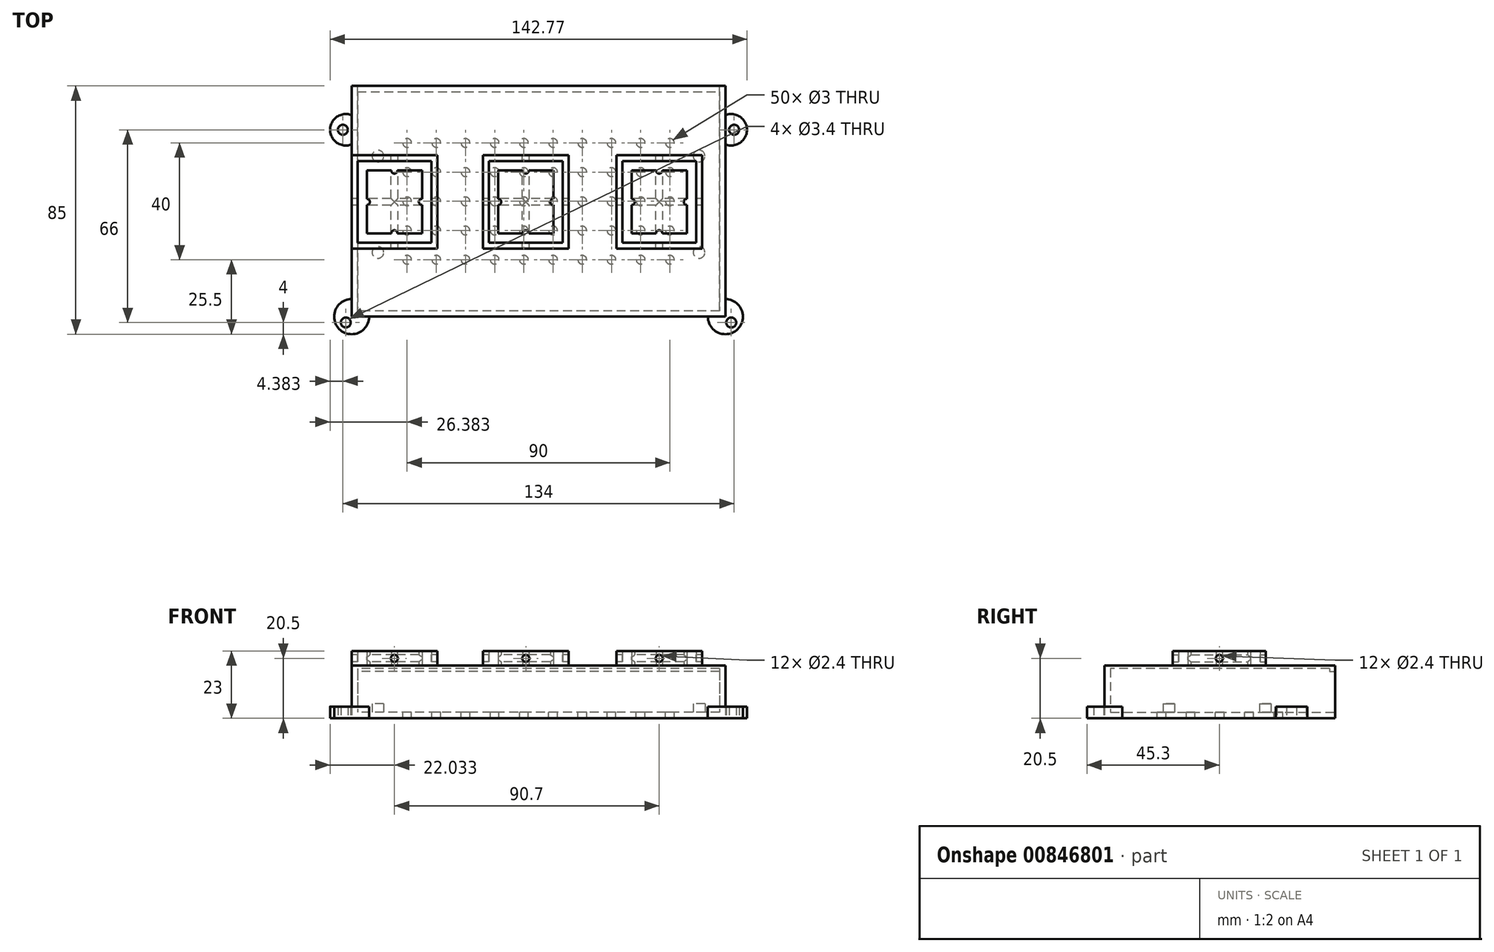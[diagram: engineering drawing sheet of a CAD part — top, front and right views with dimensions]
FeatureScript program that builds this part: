
annotation { "Feature Type Name" : "Feature", "Feature Type Description" : "" }
export const myFeature = defineFeature(function(context is Context, id is Id, definition is map)
    precondition{}
    {
        {
            var Q0;
            Q0=qCreatedBy(makeId("Top.planeOp"),FACE);
            var sketch = newSketch(context, id + "F0", { "sketchPlane" : qUnion([Q0])});
            skLineSegment(sketch, "E0.bottom", {"start": v(63.95, -38.95) * mm, "end": v(-60.05, -38.95) * mm});
            skLineSegment(sketch, "E0.top", {"start": v(63.95, 36.05) * mm, "end": v(-60.05, 36.05) * mm});
            skLineSegment(sketch, "E0.left", {"start": v(63.95, -38.95) * mm, "end": v(63.95, 36.05) * mm});
            skLineSegment(sketch, "E0.right", {"start": v(-60.05, -38.95) * mm, "end": v(-60.05, 36.05) * mm});
            skCircle(sketch, "E1", {"center": v(-53.05, 14.05) * mm, "radius": 2 * mm});
            skCircle(sketch, "E2", {"center": v(-53.05, -18.95) * mm, "radius": 2 * mm});
            skCircle(sketch, "E3", {"center": v(56.95, -18.95) * mm, "radius": 2 * mm});
            skCircle(sketch, "E4", {"center": v(56.95, 14.05) * mm, "radius": 2 * mm});
            skLineSegment(sketch, "E5.bottom", {"start": v(65.95, -40.95) * mm, "end": v(-62.05, -40.95) * mm});
            skLineSegment(sketch, "E5.top", {"start": v(65.95, 38.05) * mm, "end": v(-62.05, 38.05) * mm});
            skLineSegment(sketch, "E5.left", {"start": v(65.95, -40.95) * mm, "end": v(65.95, 38.05) * mm});
            skLineSegment(sketch, "E5.right", {"start": v(-62.05, -40.95) * mm, "end": v(-62.05, 38.05) * mm});
            skArc(sketch, "E6", {"start": v(59.95, -40.95) * mm, "mid": v(70.2, -45.2) * mm, "end": v(65.95, -34.95) * mm});
            skArc(sketch, "E7", {"start": v(-62.05, -34.95) * mm, "mid": v(-66.29, -45.2) * mm, "end": v(-56.05, -40.95) * mm});
            skPoint(sketch, "E8", {"position": v(67.95, -42.95) * mm});
            skPoint(sketch, "E9", {"position": v(-64.05, -42.95) * mm});
            skArc(sketch, "E10", {"start": v(-62.05, 28.05) * mm, "mid": v(-69.43, 23.05) * mm, "end": v(-62.05, 18.05) * mm});
            skArc(sketch, "E11", {"start": v(65.95, 18.05) * mm, "mid": v(73.34, 23.05) * mm, "end": v(65.95, 28.05) * mm});
            skPoint(sketch, "E12", {"position": v(-65.05, 23.05) * mm});
            skPoint(sketch, "E13", {"position": v(68.95, 23.05) * mm});
            skSolve(sketch);
        }
        {
            var Q0;
            Q0=makeQuery(id+"F0.imprint","IMPRINT",FACE,{"disambiguationData":[TD([[makeQuery(id+"F0.imprint","IMPRINT",EDGE,{"derivedFrom":sQuery(id+"F0.wireOp",EDGE,"E0.bottom")}),-1.0]])]});
            extrude(context, id + "F1", {"entities" : qUnion([Q0]), "depth" : 2 * mm, "offsetDistance" : 25 * mm});
        }
        {
            var Q0;
            Q0=makeQuery(id+"F0.imprint","IMPRINT",FACE,{"disambiguationData":[TD([[makeQuery(id+"F0.imprint","IMPRINT",EDGE,{"derivedFrom":sQuery(id+"F0.wireOp",EDGE,"E0.bottom")}),1.0]])]});
            extrude(context, id + "F2", {"entities" : qUnion([Q0]), "operationType" : NewBodyOperationType.ADD, "depth" : 18 * mm, "offsetDistance" : 25 * mm});
        }
        {
            var Q0;
            Q0=makeQuery(id+"F2.opExtrude","SWEPT_FACE",FACE,{"disambiguationData":[OSD([sQuery(id+"F0.wireOp",EDGE,"E5.top")])]});
            var sketch = newSketch(context, id + "F3", { "sketchPlane" : qUnion([Q0])});
            skLineSegment(sketch, "E14.bottom", {"start": v(-63.95, 16) * mm, "end": v(60.05, 16) * mm});
            skLineSegment(sketch, "E14.top", {"start": v(-63.95, 2) * mm, "end": v(60.05, 2) * mm});
            skLineSegment(sketch, "E14.left", {"start": v(-63.95, 16) * mm, "end": v(-63.95, 2) * mm});
            skLineSegment(sketch, "E14.right", {"start": v(60.05, 16) * mm, "end": v(60.05, 2) * mm});
            skSolve(sketch);
        }
        {
            var Q0;
            Q0=makeQuery(id+"F3.imprint","IMPRINT",FACE,{"disambiguationData":[TD([[makeQuery(id+"F3.imprint","IMPRINT",EDGE,{"derivedFrom":sQuery(id+"F3.wireOp",EDGE,"E14.bottom")}),-1.0]])]});
            extrude(context, id + "F4", {"entities" : qUnion([Q0]), "operationType" : NewBodyOperationType.REMOVE, "endBound" : BoundingType.UP_TO_NEXT, "oppositeDirection" : true, "depth" : 25 * mm, "offsetDistance" : 25 * mm});
        }
        {
            var Q0;
            Q0=makeQuery(id+"F0.imprint","IMPRINT",FACE,{"disambiguationData":[TD([[makeQuery(id+"F0.imprint","IMPRINT",EDGE,{"derivedFrom":sQuery(id+"F0.wireOp",EDGE,"E1")}),1.0]])]});
            var Q1;
            Q1=makeQuery(id+"F0.imprint","IMPRINT",FACE,{"disambiguationData":[TD([[makeQuery(id+"F0.imprint","IMPRINT",EDGE,{"derivedFrom":sQuery(id+"F0.wireOp",EDGE,"E2")}),1.0]])]});
            var Q2;
            Q2=makeQuery(id+"F0.imprint","IMPRINT",FACE,{"disambiguationData":[TD([[makeQuery(id+"F0.imprint","IMPRINT",EDGE,{"derivedFrom":sQuery(id+"F0.wireOp",EDGE,"E3")}),1.0]])]});
            var Q3;
            Q3=makeQuery(id+"F0.imprint","IMPRINT",FACE,{"disambiguationData":[TD([[makeQuery(id+"F0.imprint","IMPRINT",EDGE,{"derivedFrom":sQuery(id+"F0.wireOp",EDGE,"E4")}),1.0]])]});
            extrude(context, id + "F5", {"entities" : qUnion([Q0, Q1, Q2, Q3]), "operationType" : NewBodyOperationType.ADD, "depth" : 5 * mm, "offsetDistance" : 25 * mm});
        }
        {
            var Q0;
            Q0=makeQuery(id+"F2.opExtrude","SWEPT_FACE",FACE,{"disambiguationData":[OSD([sQuery(id+"F0.wireOp",EDGE,"E0.bottom")])]});
            var sketch = newSketch(context, id + "F6", { "sketchPlane" : qUnion([Q0])});
            skLineSegment(sketch, "E15.bottom", {"start": v(-63.95, 18) * mm, "end": v(60.05, 18) * mm});
            skLineSegment(sketch, "E15.top", {"start": v(-63.95, 17) * mm, "end": v(60.05, 17) * mm});
            skLineSegment(sketch, "E15.left", {"start": v(-63.95, 18) * mm, "end": v(-63.95, 17) * mm});
            skLineSegment(sketch, "E15.right", {"start": v(60.05, 18) * mm, "end": v(60.05, 17) * mm});
            skSolve(sketch);
        }
        {
            var Q0;
            Q0=makeQuery(id+"F6.imprint","IMPRINT",FACE,{"disambiguationData":[TD([[makeQuery(id+"F6.imprint","IMPRINT",EDGE,{"derivedFrom":sQuery(id+"F6.wireOp",EDGE,"E15.bottom")}),-1.0]])]});
            extrude(context, id + "F7", {"entities" : qUnion([Q0]), "operationType" : NewBodyOperationType.ADD, "endBound" : BoundingType.UP_TO_NEXT, "depth" : 25 * mm, "offsetDistance" : 25 * mm});
        }
        {
            var Q0;
            Q0=makeQuery(id+"F7.boolean.opBoolean","MERGE",FACE,{"derivedFrom":[makeQuery(id+"F2.opExtrude","CAP_FACE",FACE,{"disambiguationData":[OSD([sQuery(id+"F0.wireOp",EDGE,"E0.bottom"),sQuery(id+"F0.wireOp",EDGE,"E0.top"),sQuery(id+"F0.wireOp",EDGE,"E0.left"),sQuery(id+"F0.wireOp",EDGE,"E0.right"),sQuery(id+"F0.wireOp",EDGE,"E5.bottom"),sQuery(id+"F0.wireOp",EDGE,"E5.top"),sQuery(id+"F0.wireOp",EDGE,"E5.left"),sQuery(id+"F0.wireOp",EDGE,"E5.right")])],"isStart":false}),makeQuery(id+"F7.opExtrude","SWEPT_FACE",FACE,{"disambiguationData":[OSD([sQuery(id+"F6.wireOp",EDGE,"E15.bottom")])]})]});
            var sketch = newSketch(context, id + "F8", { "sketchPlane" : qUnion([Q0])});
            skLineSegment(sketch, "E16.bottom", {"start": v(-15.05, 12.3) * mm, "end": v(10.25, 12.3) * mm});
            skLineSegment(sketch, "E16.top", {"start": v(-15.05, -15.6) * mm, "end": v(10.25, -15.6) * mm});
            skLineSegment(sketch, "E16.left", {"start": v(-15.05, 12.3) * mm, "end": v(-15.05, -15.6) * mm});
            skLineSegment(sketch, "E16.right", {"start": v(10.25, 12.3) * mm, "end": v(10.25, -15.6) * mm});
            skLineSegment(sketch, "E17.bottom", {"start": v(-11.85, 9.1) * mm, "end": v(7.05, 9.1) * mm});
            skLineSegment(sketch, "E17.top", {"start": v(-11.85, -12.4) * mm, "end": v(7.05, -12.4) * mm});
            skLineSegment(sketch, "E17.left", {"start": v(-11.85, 9.1) * mm, "end": v(-11.85, -12.4) * mm});
            skLineSegment(sketch, "E17.right", {"start": v(7.05, 9.1) * mm, "end": v(7.05, -12.4) * mm});
            skLineSegment(sketch, "E18.bottom", {"start": v(30.65, 12.3) * mm, "end": v(55.95, 12.3) * mm});
            skLineSegment(sketch, "E18.top", {"start": v(30.65, -15.6) * mm, "end": v(55.95, -15.6) * mm});
            skLineSegment(sketch, "E18.left", {"start": v(30.65, 12.3) * mm, "end": v(30.65, -15.6) * mm});
            skLineSegment(sketch, "E18.right", {"start": v(55.95, 12.3) * mm, "end": v(55.95, -15.6) * mm});
            skLineSegment(sketch, "E19.bottom", {"start": v(33.85, 9.1) * mm, "end": v(52.75, 9.1) * mm});
            skLineSegment(sketch, "E19.top", {"start": v(33.85, -12.4) * mm, "end": v(52.75, -12.4) * mm});
            skLineSegment(sketch, "E19.left", {"start": v(33.85, 9.1) * mm, "end": v(33.85, -12.4) * mm});
            skLineSegment(sketch, "E19.right", {"start": v(52.75, 9.1) * mm, "end": v(52.75, -12.4) * mm});
            skCircle(sketch, "E20", {"center": v(-2.4, 9.1) * mm, "radius": 1.05 * mm});
            skLineSegment(sketch, "E21.bottom", {"start": v(-17.05, 14.3) * mm, "end": v(12.25, 14.3) * mm});
            skLineSegment(sketch, "E21.top", {"start": v(-17.05, -17.6) * mm, "end": v(12.25, -17.6) * mm});
            skLineSegment(sketch, "E21.left", {"start": v(-17.05, 14.3) * mm, "end": v(-17.05, -17.6) * mm});
            skLineSegment(sketch, "E21.right", {"start": v(12.25, 14.3) * mm, "end": v(12.25, -17.6) * mm});
            skLineSegment(sketch, "E22.bottom", {"start": v(28.65, 14.3) * mm, "end": v(57.95, 14.3) * mm});
            skLineSegment(sketch, "E22.top", {"start": v(28.65, -17.6) * mm, "end": v(57.95, -17.6) * mm});
            skLineSegment(sketch, "E22.left", {"start": v(28.65, 14.3) * mm, "end": v(28.65, -17.6) * mm});
            skLineSegment(sketch, "E22.right", {"start": v(57.95, 14.3) * mm, "end": v(57.95, -17.6) * mm});
            skCircle(sketch, "E23", {"center": v(7.05, -1.65) * mm, "radius": 1.05 * mm});
            skCircle(sketch, "E24", {"center": v(-2.4, -12.4) * mm, "radius": 1.05 * mm});
            skCircle(sketch, "E25", {"center": v(-11.85, -1.65) * mm, "radius": 1.05 * mm});
            skCircle(sketch, "E26", {"center": v(33.85, -1.65) * mm, "radius": 1.05 * mm});
            skCircle(sketch, "E27", {"center": v(43.3, -12.4) * mm, "radius": 1.05 * mm});
            skCircle(sketch, "E28", {"center": v(52.75, -1.65) * mm, "radius": 1.05 * mm});
            skCircle(sketch, "E29", {"center": v(43.3, 9.1) * mm, "radius": 1.05 * mm});
            skLineSegment(sketch, "E30.1.0.0", {"start": v(-56.85, 9.1) * mm, "end": v(-37.95, 9.1) * mm});
            skLineSegment(sketch, "E30.1.0.1", {"start": v(-32.75, 14.3) * mm, "end": v(-32.75, -17.6) * mm});
            skLineSegment(sketch, "E30.1.0.2", {"start": v(-62.05, -17.6) * mm, "end": v(-32.75, -17.6) * mm});
            skLineSegment(sketch, "E30.1.0.3", {"start": v(-56.85, 9.1) * mm, "end": v(-56.85, -12.4) * mm});
            skLineSegment(sketch, "E30.1.0.4", {"start": v(-62.05, 14.3) * mm, "end": v(-32.75, 14.3) * mm});
            skLineSegment(sketch, "E30.1.0.5", {"start": v(-62.05, 14.3) * mm, "end": v(-62.05, -17.6) * mm});
            skLineSegment(sketch, "E30.1.0.6", {"start": v(-56.85, -12.4) * mm, "end": v(-37.95, -12.4) * mm});
            skLineSegment(sketch, "E30.1.0.7", {"start": v(-37.95, 9.1) * mm, "end": v(-37.95, -12.4) * mm});
            skLineSegment(sketch, "E30.1.0.8", {"start": v(-34.75, 12.3) * mm, "end": v(-34.75, -15.6) * mm});
            skLineSegment(sketch, "E30.1.0.9", {"start": v(-60.05, 12.3) * mm, "end": v(-34.75, 12.3) * mm});
            skLineSegment(sketch, "E30.1.0.10", {"start": v(-60.05, 12.3) * mm, "end": v(-60.05, -15.6) * mm});
            skLineSegment(sketch, "E30.1.0.11", {"start": v(-60.05, -15.6) * mm, "end": v(-34.75, -15.6) * mm});
            skCircle(sketch, "E30.1.0.12", {"center": v(-56.85, -1.65) * mm, "radius": 1.05 * mm});
            skCircle(sketch, "E30.1.0.13", {"center": v(-47.4, -12.4) * mm, "radius": 1.05 * mm});
            skCircle(sketch, "E30.1.0.14", {"center": v(-37.95, -1.65) * mm, "radius": 1.05 * mm});
            skCircle(sketch, "E30.1.0.15", {"center": v(-47.4, 9.1) * mm, "radius": 1.05 * mm});
            skLineSegment(sketch, "E30.direction1", {"start": v(-17.05, -17.6) * mm, "end": v(-62.05, -17.6) * mm, "construction": true});
            skSolve(sketch);
        }
        {
            var Q0;
            Q0=makeQuery(id+"F8.imprint","IMPRINT",FACE,{"disambiguationData":[TD([[makeQuery(id+"F8.imprint","IMPRINT",EDGE,{"derivedFrom":sQuery(id+"F8.wireOp",EDGE,"E16.bottom")}),1.0]])]});
            var Q1;
            {var subQ1=sQuery(id+"F8.wireOp",EDGE,"E17.bottom");var subQ4=sQuery(id+"F8.wireOp",EDGE,"E17.left");var subQ5=makeQuery(id+"F8.imprint","INTERSECT",VERTEX,{"derivedFrom":[subQ1,subQ4]});Q1=makeQuery(id+"F8.imprint","IMPRINT",FACE,{"disambiguationData":[TD([[makeQuery(id+"F8.imprint","IMPRINT",EDGE,{"disambiguationData":[TD([[subQ5,-1.0]])],"derivedFrom":subQ1}),-1.0]])]});}
            var Q2;
            {var subQ1=sQuery(id+"F8.wireOp",EDGE,"E19.left");var subQ4=sQuery(id+"F8.wireOp",EDGE,"E19.bottom");var subQ5=makeQuery(id+"F8.imprint","INTERSECT",VERTEX,{"derivedFrom":[subQ4,subQ1]});Q2=makeQuery(id+"F8.imprint","IMPRINT",FACE,{"disambiguationData":[TD([[makeQuery(id+"F8.imprint","IMPRINT",EDGE,{"disambiguationData":[TD([[subQ5,-1.0]])],"derivedFrom":subQ4}),-1.0]])]});}
            var Q3;
            Q3=makeQuery(id+"F8.imprint","IMPRINT",FACE,{"disambiguationData":[TD([[makeQuery(id+"F8.imprint","IMPRINT",EDGE,{"derivedFrom":sQuery(id+"F8.wireOp",EDGE,"E18.bottom")}),1.0]])]});
            var Q4;
            {var subQ8=sQuery(id+"F8.wireOp",EDGE,"E30.1.0.3");var subQ13=sQuery(id+"F8.wireOp",EDGE,"E30.1.0.0");var subQ14=makeQuery(id+"F8.imprint","INTERSECT",VERTEX,{"derivedFrom":[subQ13,subQ8]});Q4=makeQuery(id+"F8.imprint","IMPRINT",FACE,{"disambiguationData":[TD([[makeQuery(id+"F8.imprint","IMPRINT",EDGE,{"disambiguationData":[TD([[subQ14,-1.0]])],"derivedFrom":subQ13}),-1.0]])]});}
            var Q5;
            Q5=makeQuery(id+"F8.imprint","IMPRINT",FACE,{"disambiguationData":[TD([[makeQuery(id+"F8.imprint","IMPRINT",EDGE,{"derivedFrom":sQuery(id+"F8.wireOp",EDGE,"E30.1.0.1")}),-1.0]])]});
            extrude(context, id + "F9", {"entities" : qUnion([Q0, Q1, Q2, Q3, Q4, Q5]), "operationType" : NewBodyOperationType.ADD, "depth" : 5 * mm, "offsetDistance" : 25 * mm});
        }
        {
            var Q0;
            {var subQ3=sQuery(id+"F0.wireOp",EDGE,"mSIi04YN-kxax-JNjT-FgOG-nQ7TCZ75OfZn");Q0=makeQuery(id+"F0.imprint","IMPRINT",FACE,{"disambiguationData":[TD([[makeQuery(id+"F0.imprint","IMPRINT",EDGE,{"derivedFrom":subQ3}),1.0]])]});}
            var Q1;
            {var subQ3=sQuery(id+"F0.wireOp",EDGE,"E7");Q1=makeQuery(id+"F0.imprint","IMPRINT",FACE,{"disambiguationData":[TD([[makeQuery(id+"F0.imprint","IMPRINT",EDGE,{"derivedFrom":subQ3}),1.0]])]});}
            var Q2;
            {var subQ3=sQuery(id+"F0.wireOp",EDGE,"E6");Q2=makeQuery(id+"F0.imprint","IMPRINT",FACE,{"disambiguationData":[TD([[makeQuery(id+"F0.imprint","IMPRINT",EDGE,{"derivedFrom":subQ3}),1.0]])]});}
            var Q3;
            {var subQ3=sQuery(id+"F0.wireOp",EDGE,"2plFA931-hQRt-3nQC-mfBG-ZgZCNlgZvkkJ");Q3=makeQuery(id+"F0.imprint","IMPRINT",FACE,{"disambiguationData":[TD([[makeQuery(id+"F0.imprint","IMPRINT",EDGE,{"derivedFrom":subQ3}),1.0]])]});}
            var Q4;
            {var subQ0=sQuery(id+"F0.wireOp",EDGE,"E11");Q4=makeQuery(id+"F0.imprint","IMPRINT",FACE,{"disambiguationData":[TD([[makeQuery(id+"F0.imprint","IMPRINT",EDGE,{"derivedFrom":subQ0}),1.0]])]});}
            var Q5;
            {var subQ0=sQuery(id+"F0.wireOp",EDGE,"E10");Q5=makeQuery(id+"F0.imprint","IMPRINT",FACE,{"disambiguationData":[TD([[makeQuery(id+"F0.imprint","IMPRINT",EDGE,{"derivedFrom":subQ0}),1.0]])]});}
            extrude(context, id + "F10", {"entities" : qUnion([Q0, Q1, Q2, Q3, Q4, Q5]), "operationType" : NewBodyOperationType.ADD, "depth" : 4 * mm, "offsetDistance" : 25 * mm});
        }
        {
            var Q0;
            Q0=sQuery(id+"F0.wireOp",VERTEX,"E9");
            var Q1;
            Q1=sQuery(id+"F0.wireOp",VERTEX,"E8");
            var Q2;
            Q2=sQuery(id+"F0.wireOp",VERTEX,"c99c4bf4-b353-43c5-8701-cd882d36ad5d");
            var Q3;
            Q3=sQuery(id+"F0.wireOp",VERTEX,"7333e0a9-a8a0-4818-a494-4a8ed08a8f91");
            var Q4;
            Q4=sQuery(id+"F0.wireOp",VERTEX,"E13");
            var Q5;
            Q5=sQuery(id+"F0.wireOp",VERTEX,"E12");
            var Q6;
            Q6=makeQuery(id+"F1.opExtrude","SWEPT_BODY",BODY,{"disambiguationData":[OSD([sQuery(id+"F0.wireOp",EDGE,"E0.bottom"),sQuery(id+"F0.wireOp",EDGE,"E0.top"),sQuery(id+"F0.wireOp",EDGE,"E0.left"),sQuery(id+"F0.wireOp",EDGE,"E0.right"),sQuery(id+"F0.wireOp",EDGE,"E1"),sQuery(id+"F0.wireOp",EDGE,"E2"),sQuery(id+"F0.wireOp",EDGE,"E3"),sQuery(id+"F0.wireOp",EDGE,"E4")])]});
            hole(context, id + "F11", {"style" : HoleStyle.SIMPLE, "endStyle" : HoleEndStyle.THROUGH, "oppositeDirection" : true, "standardTappedOrClearance" : lookupTablePath({ "fit" : "Normal", "standard" : "ISO", "size" : "M3", "type" : "Clearance" }), "standardBlindInLast" : lookupTablePath({ "fit" : "Normal", "standard" : "ISO", "size" : "M3", "type" : "Clearance" }), "holeDiameter" : 3.4 * mm, "majorDiameter" : 5 * mm, "isTappedThrough" : true, "tappedDepth" : 12 * mm, "tapClearance" : 3, "locations" : qUnion([Q0, Q1, Q2, Q3, Q4, Q5]), "scope" : qUnion([Q6])});
        }
        {
            var Q0;
            Q0=makeQuery(id+"F9.boolean.opBoolean","MERGE",FACE,{"derivedFrom":[makeQuery(id+"F2.opExtrude","SWEPT_FACE",FACE,{"disambiguationData":[OSD([sQuery(id+"F0.wireOp",EDGE,"E5.right")])]}),makeQuery(id+"F9.opExtrude","SWEPT_FACE",FACE,{"disambiguationData":[OSD([sQuery(id+"F8.wireOp",EDGE,"E30.1.0.5")])]})]});
            var sketch = newSketch(context, id + "F12", { "sketchPlane" : qUnion([Q0])});
            skPoint(sketch, "E31", {"position": v(1.65, 20.5) * mm});
            skPoint(sketch, "E31.positionSnap0", {"position": v(1.65, 23) * mm});
            skPoint(sketch, "E31.positionSnap1", {"position": v(-14.3, 20.5) * mm});
            skSolve(sketch);
        }
        {
            var Q0;
            Q0=sQuery(id+"F12.wireOp",VERTEX,"E31");
            var Q1;
            Q1=makeQuery(id+"F1.opExtrude","SWEPT_BODY",BODY,{"disambiguationData":[OSD([sQuery(id+"F0.wireOp",EDGE,"E0.bottom"),sQuery(id+"F0.wireOp",EDGE,"E0.top"),sQuery(id+"F0.wireOp",EDGE,"E0.left"),sQuery(id+"F0.wireOp",EDGE,"E0.right"),sQuery(id+"F0.wireOp",EDGE,"E1"),sQuery(id+"F0.wireOp",EDGE,"E2"),sQuery(id+"F0.wireOp",EDGE,"E3"),sQuery(id+"F0.wireOp",EDGE,"E4")])]});
            hole(context, id + "F13", {"style" : HoleStyle.SIMPLE, "endStyle" : HoleEndStyle.THROUGH, "holeDiameter" : 2.4 * mm, "majorDiameter" : 5 * mm, "isTappedThrough" : true, "tappedDepth" : 12 * mm, "tapClearance" : 3, "locations" : qUnion([Q0]), "scope" : qUnion([Q1])});
        }
        {
            var Q0;
            Q0=makeQuery(id+"F9.opExtrude","SWEPT_FACE",FACE,{"disambiguationData":[OSD([sQuery(id+"F8.wireOp",EDGE,"E22.bottom")])]});
            var sketch = newSketch(context, id + "F14", { "sketchPlane" : qUnion([Q0])});
            skPoint(sketch, "E32", {"position": v(-43.3, 20.5) * mm});
            skPoint(sketch, "E32.positionSnap0", {"position": v(-43.3, 23) * mm});
            skPoint(sketch, "E32.positionSnap1", {"position": v(-57.95, 20.5) * mm});
            skSolve(sketch);
        }
        {
            var Q0;
            Q0=makeQuery(id+"F9.opExtrude","SWEPT_FACE",FACE,{"disambiguationData":[OSD([sQuery(id+"F8.wireOp",EDGE,"E21.bottom")])]});
            var sketch = newSketch(context, id + "F15", { "sketchPlane" : qUnion([Q0])});
            skPoint(sketch, "E33", {"position": v(2.4, 20.5) * mm});
            skPoint(sketch, "E33.positionSnap0", {"position": v(2.4, 23) * mm});
            skPoint(sketch, "E33.positionSnap1", {"position": v(-12.25, 20.5) * mm});
            skSolve(sketch);
        }
        {
            var Q0;
            Q0=makeQuery(id+"F9.opExtrude","SWEPT_FACE",FACE,{"disambiguationData":[OSD([sQuery(id+"F8.wireOp",EDGE,"E30.1.0.4")])]});
            var sketch = newSketch(context, id + "F16", { "sketchPlane" : qUnion([Q0])});
            skPoint(sketch, "E34", {"position": v(47.4, 20.5) * mm});
            skPoint(sketch, "E34.positionSnap0", {"position": v(47.4, 23) * mm});
            skPoint(sketch, "E34.positionSnap1", {"position": v(32.75, 20.5) * mm});
            skSolve(sketch);
        }
        {
            var Q0;
            Q0=sQuery(id+"F14.wireOp",VERTEX,"E32");
            var Q1;
            Q1=sQuery(id+"F15.wireOp",VERTEX,"E33");
            var Q2;
            Q2=sQuery(id+"F16.wireOp",VERTEX,"E34");
            var Q3;
            Q3=makeQuery(id+"F1.opExtrude","SWEPT_BODY",BODY,{"disambiguationData":[OSD([sQuery(id+"F0.wireOp",EDGE,"E0.bottom"),sQuery(id+"F0.wireOp",EDGE,"E0.top"),sQuery(id+"F0.wireOp",EDGE,"E0.left"),sQuery(id+"F0.wireOp",EDGE,"E0.right"),sQuery(id+"F0.wireOp",EDGE,"E1"),sQuery(id+"F0.wireOp",EDGE,"E2"),sQuery(id+"F0.wireOp",EDGE,"E3"),sQuery(id+"F0.wireOp",EDGE,"E4")])]});
            hole(context, id + "F17", {"style" : HoleStyle.SIMPLE, "endStyle" : HoleEndStyle.THROUGH, "holeDiameter" : 2.4 * mm, "majorDiameter" : 5 * mm, "isTappedThrough" : true, "tappedDepth" : 12 * mm, "tapClearance" : 3, "locations" : qUnion([Q0, Q1, Q2]), "scope" : qUnion([Q3])});
        }
        {
            var Q0;
            Q0=makeQuery(id+"F4.boolean.opBoolean","MERGE",FACE,{"derivedFrom":[makeQuery(id+"F1.opExtrude","CAP_FACE",FACE,{"disambiguationData":[OSD([sQuery(id+"F0.wireOp",EDGE,"E0.bottom"),sQuery(id+"F0.wireOp",EDGE,"E0.top"),sQuery(id+"F0.wireOp",EDGE,"E0.left"),sQuery(id+"F0.wireOp",EDGE,"E0.right"),sQuery(id+"F0.wireOp",EDGE,"E1"),sQuery(id+"F0.wireOp",EDGE,"E2"),sQuery(id+"F0.wireOp",EDGE,"E3"),sQuery(id+"F0.wireOp",EDGE,"E4")])],"isStart":false})],"fromTools":[makeQuery(id+"F4.opExtrude","SWEPT_FACE",FACE,{"disambiguationData":[OSD([sQuery(id+"F3.wireOp",EDGE,"E14.top")])]})]});
            var sketch = newSketch(context, id + "F18", { "sketchPlane" : qUnion([Q0])});
            skCircle(sketch, "E35", {"center": v(46.95, -21.45) * mm, "radius": 1.5 * mm});
            skCircle(sketch, "E36.0.1.0", {"center": v(46.95, -11.45) * mm, "radius": 1.5 * mm});
            skCircle(sketch, "E36.0.2.0", {"center": v(46.95, -1.45) * mm, "radius": 1.5 * mm});
            skCircle(sketch, "E36.0.3.0", {"center": v(46.95, 8.55) * mm, "radius": 1.5 * mm});
            skCircle(sketch, "E36.0.4.0", {"center": v(46.95, 18.55) * mm, "radius": 1.5 * mm});
            skCircle(sketch, "E36.1.0.0", {"center": v(36.95, -21.45) * mm, "radius": 1.5 * mm});
            skCircle(sketch, "E36.1.1.0", {"center": v(36.95, -11.45) * mm, "radius": 1.5 * mm});
            skCircle(sketch, "E36.1.2.0", {"center": v(36.95, -1.45) * mm, "radius": 1.5 * mm});
            skCircle(sketch, "E36.1.3.0", {"center": v(36.95, 8.55) * mm, "radius": 1.5 * mm});
            skCircle(sketch, "E36.1.4.0", {"center": v(36.95, 18.55) * mm, "radius": 1.5 * mm});
            skCircle(sketch, "E36.2.0.0", {"center": v(26.95, -21.45) * mm, "radius": 1.5 * mm});
            skCircle(sketch, "E36.2.1.0", {"center": v(26.95, -11.45) * mm, "radius": 1.5 * mm});
            skCircle(sketch, "E36.2.2.0", {"center": v(26.95, -1.45) * mm, "radius": 1.5 * mm});
            skCircle(sketch, "E36.2.3.0", {"center": v(26.95, 8.55) * mm, "radius": 1.5 * mm});
            skCircle(sketch, "E36.2.4.0", {"center": v(26.95, 18.55) * mm, "radius": 1.5 * mm});
            skCircle(sketch, "E36.3.0.0", {"center": v(16.95, -21.45) * mm, "radius": 1.5 * mm});
            skCircle(sketch, "E36.3.1.0", {"center": v(16.95, -11.45) * mm, "radius": 1.5 * mm});
            skCircle(sketch, "E36.3.2.0", {"center": v(16.95, -1.45) * mm, "radius": 1.5 * mm});
            skCircle(sketch, "E36.3.3.0", {"center": v(16.95, 8.55) * mm, "radius": 1.5 * mm});
            skCircle(sketch, "E36.3.4.0", {"center": v(16.95, 18.55) * mm, "radius": 1.5 * mm});
            skCircle(sketch, "E36.4.0.0", {"center": v(6.95, -21.45) * mm, "radius": 1.5 * mm});
            skCircle(sketch, "E36.4.1.0", {"center": v(6.95, -11.45) * mm, "radius": 1.5 * mm});
            skCircle(sketch, "E36.4.2.0", {"center": v(6.95, -1.45) * mm, "radius": 1.5 * mm});
            skCircle(sketch, "E36.4.3.0", {"center": v(6.95, 8.55) * mm, "radius": 1.5 * mm});
            skCircle(sketch, "E36.4.4.0", {"center": v(6.95, 18.55) * mm, "radius": 1.5 * mm});
            skCircle(sketch, "E36.5.0.0", {"center": v(-3.05, -21.45) * mm, "radius": 1.5 * mm});
            skCircle(sketch, "E36.5.1.0", {"center": v(-3.05, -11.45) * mm, "radius": 1.5 * mm});
            skCircle(sketch, "E36.5.2.0", {"center": v(-3.05, -1.45) * mm, "radius": 1.5 * mm});
            skCircle(sketch, "E36.5.3.0", {"center": v(-3.05, 8.55) * mm, "radius": 1.5 * mm});
            skCircle(sketch, "E36.5.4.0", {"center": v(-3.05, 18.55) * mm, "radius": 1.5 * mm});
            skCircle(sketch, "E36.6.0.0", {"center": v(-13.05, -21.45) * mm, "radius": 1.5 * mm});
            skCircle(sketch, "E36.6.1.0", {"center": v(-13.05, -11.45) * mm, "radius": 1.5 * mm});
            skCircle(sketch, "E36.6.2.0", {"center": v(-13.05, -1.45) * mm, "radius": 1.5 * mm});
            skCircle(sketch, "E36.6.3.0", {"center": v(-13.05, 8.55) * mm, "radius": 1.5 * mm});
            skCircle(sketch, "E36.6.4.0", {"center": v(-13.05, 18.55) * mm, "radius": 1.5 * mm});
            skCircle(sketch, "E36.7.0.0", {"center": v(-23.05, -21.45) * mm, "radius": 1.5 * mm});
            skCircle(sketch, "E36.7.1.0", {"center": v(-23.05, -11.45) * mm, "radius": 1.5 * mm});
            skCircle(sketch, "E36.7.2.0", {"center": v(-23.05, -1.45) * mm, "radius": 1.5 * mm});
            skCircle(sketch, "E36.7.3.0", {"center": v(-23.05, 8.55) * mm, "radius": 1.5 * mm});
            skCircle(sketch, "E36.7.4.0", {"center": v(-23.05, 18.55) * mm, "radius": 1.5 * mm});
            skCircle(sketch, "E36.8.0.0", {"center": v(-33.05, -21.45) * mm, "radius": 1.5 * mm});
            skCircle(sketch, "E36.8.1.0", {"center": v(-33.05, -11.45) * mm, "radius": 1.5 * mm});
            skCircle(sketch, "E36.8.2.0", {"center": v(-33.05, -1.45) * mm, "radius": 1.5 * mm});
            skCircle(sketch, "E36.8.3.0", {"center": v(-33.05, 8.55) * mm, "radius": 1.5 * mm});
            skCircle(sketch, "E36.8.4.0", {"center": v(-33.05, 18.55) * mm, "radius": 1.5 * mm});
            skCircle(sketch, "E36.9.0.0", {"center": v(-43.05, -21.45) * mm, "radius": 1.5 * mm});
            skCircle(sketch, "E36.9.1.0", {"center": v(-43.05, -11.45) * mm, "radius": 1.5 * mm});
            skCircle(sketch, "E36.9.2.0", {"center": v(-43.05, -1.45) * mm, "radius": 1.5 * mm});
            skCircle(sketch, "E36.9.3.0", {"center": v(-43.05, 8.55) * mm, "radius": 1.5 * mm});
            skCircle(sketch, "E36.9.4.0", {"center": v(-43.05, 18.55) * mm, "radius": 1.5 * mm});
            skLineSegment(sketch, "E36.direction1", {"start": v(46.95, -21.45) * mm, "end": v(36.95, -21.45) * mm, "construction": true});
            skLineSegment(sketch, "E36.direction2", {"start": v(46.95, -21.45) * mm, "end": v(46.95, -11.45) * mm, "construction": true});
            skSolve(sketch);
        }
        {
            var Q0;
            Q0=makeQuery(id+"F18.imprint","IMPRINT",FACE,{"disambiguationData":[TD([[makeQuery(id+"F18.imprint","IMPRINT",EDGE,{"derivedFrom":sQuery(id+"F18.wireOp",EDGE,"E35")}),1.0]])]});
            var Q1;
            Q1=makeQuery(id+"F18.imprint","IMPRINT",FACE,{"disambiguationData":[TD([[makeQuery(id+"F18.imprint","IMPRINT",EDGE,{"derivedFrom":sQuery(id+"F18.wireOp",EDGE,"E36.1.0.0")}),1.0]])]});
            var Q2;
            Q2=makeQuery(id+"F18.imprint","IMPRINT",FACE,{"disambiguationData":[TD([[makeQuery(id+"F18.imprint","IMPRINT",EDGE,{"derivedFrom":sQuery(id+"F18.wireOp",EDGE,"E36.2.0.0")}),1.0]])]});
            var Q3;
            Q3=makeQuery(id+"F18.imprint","IMPRINT",FACE,{"disambiguationData":[TD([[makeQuery(id+"F18.imprint","IMPRINT",EDGE,{"derivedFrom":sQuery(id+"F18.wireOp",EDGE,"E36.3.0.0")}),1.0]])]});
            var Q4;
            Q4=makeQuery(id+"F18.imprint","IMPRINT",FACE,{"disambiguationData":[TD([[makeQuery(id+"F18.imprint","IMPRINT",EDGE,{"derivedFrom":sQuery(id+"F18.wireOp",EDGE,"E36.4.0.0")}),1.0]])]});
            var Q5;
            Q5=makeQuery(id+"F18.imprint","IMPRINT",FACE,{"disambiguationData":[TD([[makeQuery(id+"F18.imprint","IMPRINT",EDGE,{"derivedFrom":sQuery(id+"F18.wireOp",EDGE,"E36.5.0.0")}),1.0]])]});
            var Q6;
            Q6=makeQuery(id+"F18.imprint","IMPRINT",FACE,{"disambiguationData":[TD([[makeQuery(id+"F18.imprint","IMPRINT",EDGE,{"derivedFrom":sQuery(id+"F18.wireOp",EDGE,"E36.6.0.0")}),1.0]])]});
            var Q7;
            Q7=makeQuery(id+"F18.imprint","IMPRINT",FACE,{"disambiguationData":[TD([[makeQuery(id+"F18.imprint","IMPRINT",EDGE,{"derivedFrom":sQuery(id+"F18.wireOp",EDGE,"E36.7.0.0")}),1.0]])]});
            var Q8;
            Q8=makeQuery(id+"F18.imprint","IMPRINT",FACE,{"disambiguationData":[TD([[makeQuery(id+"F18.imprint","IMPRINT",EDGE,{"derivedFrom":sQuery(id+"F18.wireOp",EDGE,"E36.8.0.0")}),1.0]])]});
            var Q9;
            Q9=makeQuery(id+"F18.imprint","IMPRINT",FACE,{"disambiguationData":[TD([[makeQuery(id+"F18.imprint","IMPRINT",EDGE,{"derivedFrom":sQuery(id+"F18.wireOp",EDGE,"E36.9.0.0")}),1.0]])]});
            var Q10;
            Q10=makeQuery(id+"F18.imprint","IMPRINT",FACE,{"disambiguationData":[TD([[makeQuery(id+"F18.imprint","IMPRINT",EDGE,{"derivedFrom":sQuery(id+"F18.wireOp",EDGE,"E36.9.1.0")}),1.0]])]});
            var Q11;
            Q11=makeQuery(id+"F18.imprint","IMPRINT",FACE,{"disambiguationData":[TD([[makeQuery(id+"F18.imprint","IMPRINT",EDGE,{"derivedFrom":sQuery(id+"F18.wireOp",EDGE,"E36.8.1.0")}),1.0]])]});
            var Q12;
            Q12=makeQuery(id+"F18.imprint","IMPRINT",FACE,{"disambiguationData":[TD([[makeQuery(id+"F18.imprint","IMPRINT",EDGE,{"derivedFrom":sQuery(id+"F18.wireOp",EDGE,"E36.7.1.0")}),1.0]])]});
            var Q13;
            Q13=makeQuery(id+"F18.imprint","IMPRINT",FACE,{"disambiguationData":[TD([[makeQuery(id+"F18.imprint","IMPRINT",EDGE,{"derivedFrom":sQuery(id+"F18.wireOp",EDGE,"E36.6.1.0")}),1.0]])]});
            var Q14;
            Q14=makeQuery(id+"F18.imprint","IMPRINT",FACE,{"disambiguationData":[TD([[makeQuery(id+"F18.imprint","IMPRINT",EDGE,{"derivedFrom":sQuery(id+"F18.wireOp",EDGE,"E36.5.1.0")}),1.0]])]});
            var Q15;
            Q15=makeQuery(id+"F18.imprint","IMPRINT",FACE,{"disambiguationData":[TD([[makeQuery(id+"F18.imprint","IMPRINT",EDGE,{"derivedFrom":sQuery(id+"F18.wireOp",EDGE,"E36.4.1.0")}),1.0]])]});
            var Q16;
            Q16=makeQuery(id+"F18.imprint","IMPRINT",FACE,{"disambiguationData":[TD([[makeQuery(id+"F18.imprint","IMPRINT",EDGE,{"derivedFrom":sQuery(id+"F18.wireOp",EDGE,"E36.3.1.0")}),1.0]])]});
            var Q17;
            Q17=makeQuery(id+"F18.imprint","IMPRINT",FACE,{"disambiguationData":[TD([[makeQuery(id+"F18.imprint","IMPRINT",EDGE,{"derivedFrom":sQuery(id+"F18.wireOp",EDGE,"E36.2.1.0")}),1.0]])]});
            var Q18;
            Q18=makeQuery(id+"F18.imprint","IMPRINT",FACE,{"disambiguationData":[TD([[makeQuery(id+"F18.imprint","IMPRINT",EDGE,{"derivedFrom":sQuery(id+"F18.wireOp",EDGE,"E36.1.1.0")}),1.0]])]});
            var Q19;
            Q19=makeQuery(id+"F18.imprint","IMPRINT",FACE,{"disambiguationData":[TD([[makeQuery(id+"F18.imprint","IMPRINT",EDGE,{"derivedFrom":sQuery(id+"F18.wireOp",EDGE,"E36.0.1.0")}),1.0]])]});
            var Q20;
            Q20=makeQuery(id+"F18.imprint","IMPRINT",FACE,{"disambiguationData":[TD([[makeQuery(id+"F18.imprint","IMPRINT",EDGE,{"derivedFrom":sQuery(id+"F18.wireOp",EDGE,"E36.0.2.0")}),1.0]])]});
            var Q21;
            Q21=makeQuery(id+"F18.imprint","IMPRINT",FACE,{"disambiguationData":[TD([[makeQuery(id+"F18.imprint","IMPRINT",EDGE,{"derivedFrom":sQuery(id+"F18.wireOp",EDGE,"E36.1.2.0")}),1.0]])]});
            var Q22;
            Q22=makeQuery(id+"F18.imprint","IMPRINT",FACE,{"disambiguationData":[TD([[makeQuery(id+"F18.imprint","IMPRINT",EDGE,{"derivedFrom":sQuery(id+"F18.wireOp",EDGE,"E36.2.2.0")}),1.0]])]});
            var Q23;
            Q23=makeQuery(id+"F18.imprint","IMPRINT",FACE,{"disambiguationData":[TD([[makeQuery(id+"F18.imprint","IMPRINT",EDGE,{"derivedFrom":sQuery(id+"F18.wireOp",EDGE,"E36.3.2.0")}),1.0]])]});
            var Q24;
            Q24=makeQuery(id+"F18.imprint","IMPRINT",FACE,{"disambiguationData":[TD([[makeQuery(id+"F18.imprint","IMPRINT",EDGE,{"derivedFrom":sQuery(id+"F18.wireOp",EDGE,"E36.4.2.0")}),1.0]])]});
            var Q25;
            Q25=makeQuery(id+"F18.imprint","IMPRINT",FACE,{"disambiguationData":[TD([[makeQuery(id+"F18.imprint","IMPRINT",EDGE,{"derivedFrom":sQuery(id+"F18.wireOp",EDGE,"E36.5.2.0")}),1.0]])]});
            var Q26;
            Q26=makeQuery(id+"F18.imprint","IMPRINT",FACE,{"disambiguationData":[TD([[makeQuery(id+"F18.imprint","IMPRINT",EDGE,{"derivedFrom":sQuery(id+"F18.wireOp",EDGE,"E36.6.2.0")}),1.0]])]});
            var Q27;
            Q27=makeQuery(id+"F18.imprint","IMPRINT",FACE,{"disambiguationData":[TD([[makeQuery(id+"F18.imprint","IMPRINT",EDGE,{"derivedFrom":sQuery(id+"F18.wireOp",EDGE,"E36.7.2.0")}),1.0]])]});
            var Q28;
            Q28=makeQuery(id+"F18.imprint","IMPRINT",FACE,{"disambiguationData":[TD([[makeQuery(id+"F18.imprint","IMPRINT",EDGE,{"derivedFrom":sQuery(id+"F18.wireOp",EDGE,"E36.8.2.0")}),1.0]])]});
            var Q29;
            Q29=makeQuery(id+"F18.imprint","IMPRINT",FACE,{"disambiguationData":[TD([[makeQuery(id+"F18.imprint","IMPRINT",EDGE,{"derivedFrom":sQuery(id+"F18.wireOp",EDGE,"E36.9.2.0")}),1.0]])]});
            var Q30;
            Q30=makeQuery(id+"F18.imprint","IMPRINT",FACE,{"disambiguationData":[TD([[makeQuery(id+"F18.imprint","IMPRINT",EDGE,{"derivedFrom":sQuery(id+"F18.wireOp",EDGE,"E36.9.3.0")}),1.0]])]});
            var Q31;
            Q31=makeQuery(id+"F18.imprint","IMPRINT",FACE,{"disambiguationData":[TD([[makeQuery(id+"F18.imprint","IMPRINT",EDGE,{"derivedFrom":sQuery(id+"F18.wireOp",EDGE,"E36.8.3.0")}),1.0]])]});
            var Q32;
            Q32=makeQuery(id+"F18.imprint","IMPRINT",FACE,{"disambiguationData":[TD([[makeQuery(id+"F18.imprint","IMPRINT",EDGE,{"derivedFrom":sQuery(id+"F18.wireOp",EDGE,"E36.7.3.0")}),1.0]])]});
            var Q33;
            Q33=makeQuery(id+"F18.imprint","IMPRINT",FACE,{"disambiguationData":[TD([[makeQuery(id+"F18.imprint","IMPRINT",EDGE,{"derivedFrom":sQuery(id+"F18.wireOp",EDGE,"E36.6.3.0")}),1.0]])]});
            var Q34;
            Q34=makeQuery(id+"F18.imprint","IMPRINT",FACE,{"disambiguationData":[TD([[makeQuery(id+"F18.imprint","IMPRINT",EDGE,{"derivedFrom":sQuery(id+"F18.wireOp",EDGE,"E36.5.3.0")}),1.0]])]});
            var Q35;
            Q35=makeQuery(id+"F18.imprint","IMPRINT",FACE,{"disambiguationData":[TD([[makeQuery(id+"F18.imprint","IMPRINT",EDGE,{"derivedFrom":sQuery(id+"F18.wireOp",EDGE,"E36.4.3.0")}),1.0]])]});
            var Q36;
            Q36=makeQuery(id+"F18.imprint","IMPRINT",FACE,{"disambiguationData":[TD([[makeQuery(id+"F18.imprint","IMPRINT",EDGE,{"derivedFrom":sQuery(id+"F18.wireOp",EDGE,"E36.3.3.0")}),1.0]])]});
            var Q37;
            Q37=makeQuery(id+"F18.imprint","IMPRINT",FACE,{"disambiguationData":[TD([[makeQuery(id+"F18.imprint","IMPRINT",EDGE,{"derivedFrom":sQuery(id+"F18.wireOp",EDGE,"E36.2.3.0")}),1.0]])]});
            var Q38;
            Q38=makeQuery(id+"F18.imprint","IMPRINT",FACE,{"disambiguationData":[TD([[makeQuery(id+"F18.imprint","IMPRINT",EDGE,{"derivedFrom":sQuery(id+"F18.wireOp",EDGE,"E36.1.3.0")}),1.0]])]});
            var Q39;
            Q39=makeQuery(id+"F18.imprint","IMPRINT",FACE,{"disambiguationData":[TD([[makeQuery(id+"F18.imprint","IMPRINT",EDGE,{"derivedFrom":sQuery(id+"F18.wireOp",EDGE,"E36.0.3.0")}),1.0]])]});
            var Q40;
            Q40=makeQuery(id+"F18.imprint","IMPRINT",FACE,{"disambiguationData":[TD([[makeQuery(id+"F18.imprint","IMPRINT",EDGE,{"derivedFrom":sQuery(id+"F18.wireOp",EDGE,"E36.0.4.0")}),1.0]])]});
            var Q41;
            Q41=makeQuery(id+"F18.imprint","IMPRINT",FACE,{"disambiguationData":[TD([[makeQuery(id+"F18.imprint","IMPRINT",EDGE,{"derivedFrom":sQuery(id+"F18.wireOp",EDGE,"E36.1.4.0")}),1.0]])]});
            var Q42;
            Q42=makeQuery(id+"F18.imprint","IMPRINT",FACE,{"disambiguationData":[TD([[makeQuery(id+"F18.imprint","IMPRINT",EDGE,{"derivedFrom":sQuery(id+"F18.wireOp",EDGE,"E36.2.4.0")}),1.0]])]});
            var Q43;
            Q43=makeQuery(id+"F18.imprint","IMPRINT",FACE,{"disambiguationData":[TD([[makeQuery(id+"F18.imprint","IMPRINT",EDGE,{"derivedFrom":sQuery(id+"F18.wireOp",EDGE,"E36.3.4.0")}),1.0]])]});
            var Q44;
            Q44=makeQuery(id+"F18.imprint","IMPRINT",FACE,{"disambiguationData":[TD([[makeQuery(id+"F18.imprint","IMPRINT",EDGE,{"derivedFrom":sQuery(id+"F18.wireOp",EDGE,"E36.4.4.0")}),1.0]])]});
            var Q45;
            Q45=makeQuery(id+"F18.imprint","IMPRINT",FACE,{"disambiguationData":[TD([[makeQuery(id+"F18.imprint","IMPRINT",EDGE,{"derivedFrom":sQuery(id+"F18.wireOp",EDGE,"E36.5.4.0")}),1.0]])]});
            var Q46;
            Q46=makeQuery(id+"F18.imprint","IMPRINT",FACE,{"disambiguationData":[TD([[makeQuery(id+"F18.imprint","IMPRINT",EDGE,{"derivedFrom":sQuery(id+"F18.wireOp",EDGE,"E36.6.4.0")}),1.0]])]});
            var Q47;
            Q47=makeQuery(id+"F18.imprint","IMPRINT",FACE,{"disambiguationData":[TD([[makeQuery(id+"F18.imprint","IMPRINT",EDGE,{"derivedFrom":sQuery(id+"F18.wireOp",EDGE,"E36.7.4.0")}),1.0]])]});
            var Q48;
            Q48=makeQuery(id+"F18.imprint","IMPRINT",FACE,{"disambiguationData":[TD([[makeQuery(id+"F18.imprint","IMPRINT",EDGE,{"derivedFrom":sQuery(id+"F18.wireOp",EDGE,"E36.8.4.0")}),1.0]])]});
            var Q49;
            Q49=makeQuery(id+"F18.imprint","IMPRINT",FACE,{"disambiguationData":[TD([[makeQuery(id+"F18.imprint","IMPRINT",EDGE,{"derivedFrom":sQuery(id+"F18.wireOp",EDGE,"E36.9.4.0")}),1.0]])]});
            extrude(context, id + "F19", {"entities" : qUnion([Q0, Q1, Q2, Q3, Q4, Q5, Q6, Q7, Q8, Q9, Q10, Q11, Q12, Q13, Q14, Q15, Q16, Q17, Q18, Q19, Q20, Q21, Q22, Q23, Q24, Q25, Q26, Q27, Q28, Q29, Q30, Q31, Q32, Q33, Q34, Q35, Q36, Q37, Q38, Q39, Q40, Q41, Q42, Q43, Q44, Q45, Q46, Q47, Q48, Q49]), "operationType" : NewBodyOperationType.REMOVE, "endBound" : BoundingType.UP_TO_NEXT, "oppositeDirection" : true, "depth" : 25 * mm, "offsetDistance" : 25 * mm});
        }
    });
